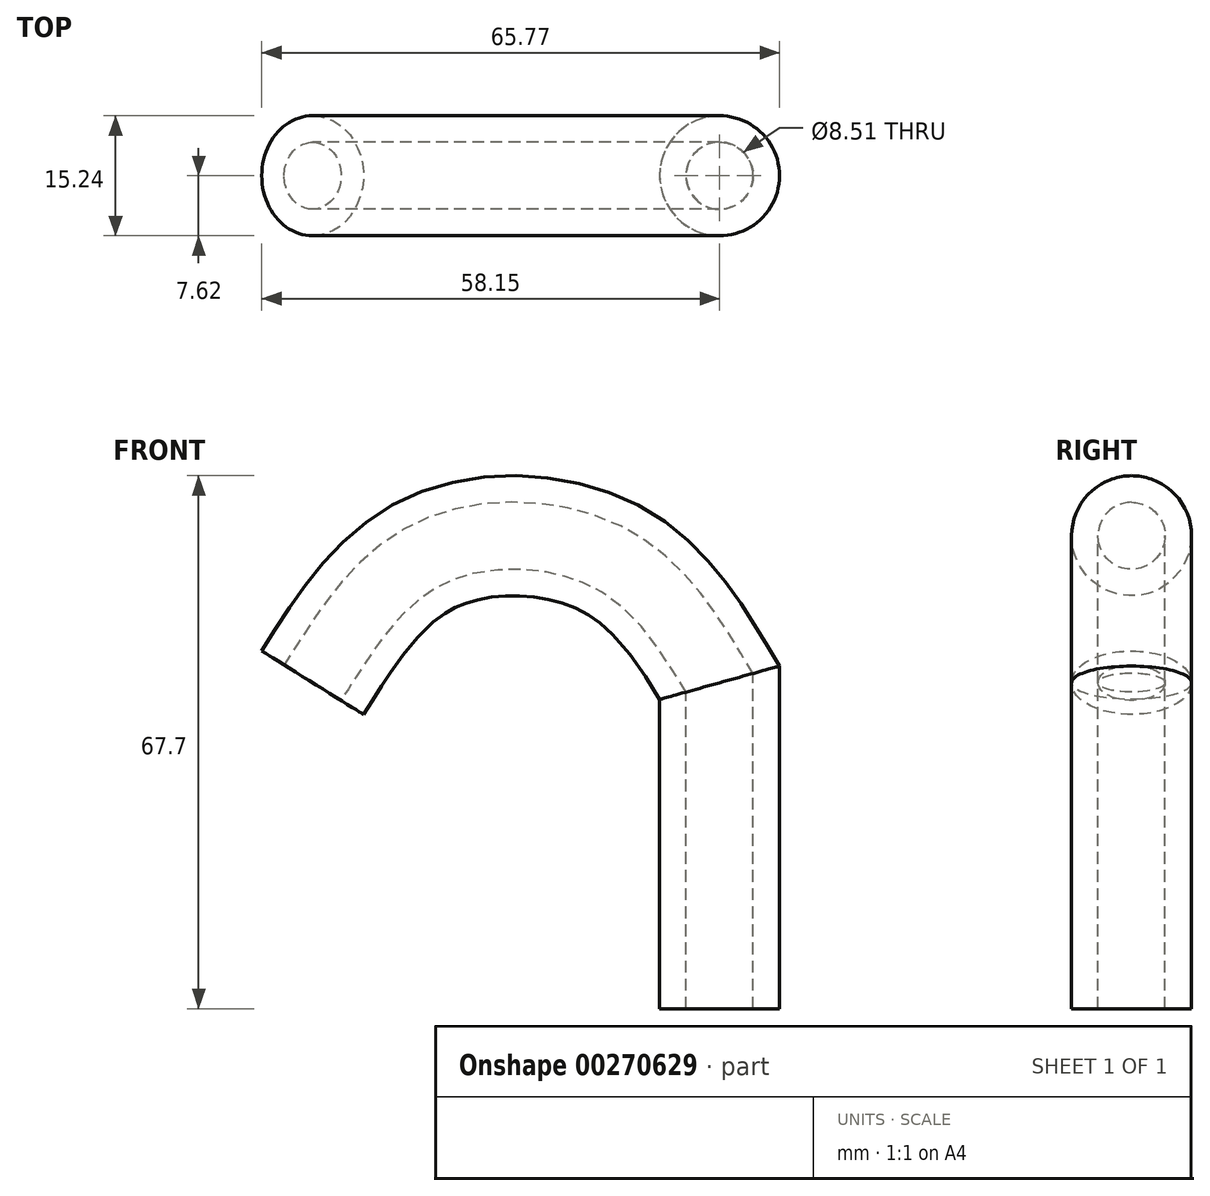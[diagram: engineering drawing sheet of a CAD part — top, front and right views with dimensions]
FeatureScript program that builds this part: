
annotation { "Feature Type Name" : "Feature", "Feature Type Description" : "" }
export const myFeature = defineFeature(function(context is Context, id is Id, definition is map)
    precondition{}
    {
        {
            var Q0;
            Q0=qCreatedBy(makeId("Top.planeOp"),FACE);
            var sketch = newSketch(context, id + "F0", { "sketchPlane" : qUnion([Q0])});
            skCircle(sketch, "E0", {"center": v(0, 0) * mm, "radius": 7.62 * mm});
            skCircle(sketch, "E1", {"center": v(0, 0) * mm, "radius": 4.26 * mm});
            skSolve(sketch);
        }
        {
            var Q0;
            Q0=qCreatedBy(makeId("Front.planeOp"),FACE);
            var sketch = newSketch(context, id + "F1", { "sketchPlane" : qUnion([Q0])});
            skLineSegment(sketch, "E2", {"start": v(0, 0) * mm, "end": v(0, 41.4) * mm});
            skFitSpline(sketch, "E3", {"points": [v(0, 41.4) * mm, v(-13.7, 57.11) * mm, v(-36.55, 57.97) * mm, v(-51.69, 41.4) * mm], "startDerivative": vector(-34.3, 57.04) * mm, "endDerivative": vector(-37.37, -59.9) * mm});
            skSolve(sketch);
        }
        {
            var Q0;
            Q0=makeQuery(id+"F0.imprint","IMPRINT",FACE,{"disambiguationData":[TD([[makeQuery(id+"F0.imprint","IMPRINT",EDGE,{"derivedFrom":sQuery(id+"F0.wireOp",EDGE,"E0")}),1.0]])]});
            var Q1;
            Q1=sQuery(id+"F1.wireOp",EDGE,"E2");
            var Q2;
            Q2=sQuery(id+"F1.wireOp",EDGE,"E3");
            sweep(context, id + "F2", {"profiles" : qUnion([Q0]), "path" : qUnion([Q1, Q2])});
        }
    });
